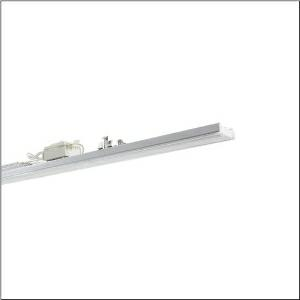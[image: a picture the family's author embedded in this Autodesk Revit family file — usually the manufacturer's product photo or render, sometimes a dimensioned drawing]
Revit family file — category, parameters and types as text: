
# Revit family: licross_r__11_recessed_ho_51tl18cn4c5m_47ff
name_source: partatom
category: Lighting Fixtures
units: mm (PartAtom-declared; Revit-internal decimal feet)

## family parameters
Cut with Voids When Loaded = No
Host = Face
Light Source = No
Part Type = Normal
Room Calculation Point = No
Round Connector Dimension = Use Diameter
Shared = No

## types (1)
- --- (1 x LED, 12610 lm, 66.5 W, 4000K)
    Apparent Load = 67 VA
    CIE Flux Codes = 78 94 99 100 100
    Color Rendering = 80
    Color Temperature = 4000K
    Default Elevation = 1800 mm
    Description = Licross® 11 Recessed HO, luminaire insert, of sheet steel, coil coated, white, length: 1.500mm, width: 66mm, height: 67mm, LED rated luminous flux: 12.610lm, light colour: 840, control gear: ON/OFF Multilumen, CLOi, with plug, 3-pole, with phase selection, mains connection: 220..240V, AC, 50/60Hz, start of lifetime: 67W, end of service life: 75W, internal wiring halogen-free, primary light control with lens, of plastic, primary optical cover: cover, of PMMA, light emission: direct distribution, primary light characteristic: symmetric, protection rating (complete): IP40, insulation class (complete): insulation class I (protective earthing), certification: CE, ENEC, VDE, UKCA, protection symbol: D if used in an environment without relevant dust loads with corresponding accessories, impact resistance: IK06, permissible ambient temperature for indoor applications: -35..+35°C, corresponds to IFS (International Featured Standards) requirements for safety and quality in the food industry, reducing of maximum allowable ambient temperature of 5°C with ceiling mounting, LABS conformity tested according to VDMA 24364:2018-05, packaging unit: 1 piece
    Height = 58 mm
    Lamp = 1 x LED
    Lamp Light Flux = 12610 lm
    Lamp Power = 66.5 W
    Lamp count = 1
    Length = 1500 mm
    Luminous efficacy = 190 lm/W
    Manufacturer = Siteco
    ModVariant = No
    Model = 51TL18CN4C5M
    Mounting Place = Ceiling
    Mounting Type = Pendant
    Number of Poles = 1
    OnlyDefault = Yes
    Power Factor = 1
    Product Name = Licross® 11 Recessed HO
    Product group = luminaire insert | ceiling pendant
    ProductGroupID = 902
    Protection Class = Protection class I
    Protection Degree = IP 40
    RLX_Detail_Level = 1
    RLX_Emergency_Light_Flux = 0 lm
    RLX_Emergency_Type = 0
    RLX_Emergency_Type_DB = No
    RlxData = <blob elided: 22309 chars, md5=1cf979aa>
    Socket = socket
    Standby Power = 0 W
    System Light Flux = 12610 lm
    System Power = 67 W
    Type Comments = factory setting: luminous flux: 100 % | (A | C | E) | 156 mA
    Type Image = l_1296930.jpg
    URL = http://relux.com
    VarID = @adj_106199
    Voltage = 0 V
    Weight = 0.00 kg
    Width = 66 mm

## geometry (parser evidence)
native form markers: Blend x4, Sweep x10
no freeform markers — native parametric forms only
